# Revit family: Closet_Support_0250D_JRSmith
name_source: partatom
category: Plumbing Fixtures
revit_build: Autodesk Revit MEP 2012 (Build: 20110309_2315(x64)
units: mm (PartAtom-declared; Revit-internal decimal feet)

## types (5) — shared parameters
04 CSI = 22 05 29
95 CSI = 15050
Assembly Code = D2010120
Capacity = 300lb
Caulk Connection = Yes
Default Elevation = 0"
Description = Compact Fixture Supports with Vertical Offset Fittings for Siphon Jet Water Closets
E = 11 1/2"
Fixture Offset = 0"
LEED = Yes
Manufacturer = Jay R. Smith Mfg. Co.
Material = Cast Iron
Material Finish = Duco coated
No-Hub Connection = Yes
Offset From Base = 9"
OmniClass Code = 22-22 42 13
OmniClass Title = Commercial Water Closets, Urinals, and Bidets
Product URL = http://www.jrsmith.com
Radius = 3"
SMARTBIM Object Version = 3
SMARTBIM URL = www.smartbim.com
Stud Length = 9"
Technical and Installation = http://www.jrsmith.com
URL = http://www.jrsmith.com
Vent Connection = Yes
Vent Radius = 1 1/8"
Warranty = 1 year material and workmanship
zero-valued in all types: Max.Static Load Lbs

## per-type parameters (varying)
| type | Barrel Base | Inner Radius | Model | Nipple Length | Pipe Diameter | Pipe Diameter2 | Pipe Radius 1 | Pipe Radius 2 | Top Pipe Radius | Weight (lb) |
| 0250DY-5X5 | 4 1/2" | 2 1/4" | 0250Y-6X5 | 11 1/2" | 5" | 5" | 2 1/2" | 2 1/2" | 1 1/4" | 145.5 |
| 0250DY-6X4 | 4 1/2" | 2 3/4" | 0250Y-6X4 | 11 1/2" | 6" | 4" | 3" | 2" | 1 1/2" | 145.5 |
| 0250DY-4X4 | 4" | 1 3/4" | 0250Y-4X4 | 9" | 4" | 4" | 2" | 2" | 1" | 120.9 |
| 0250DY-6X5 | 4 1/2" | 2 3/4" | 0250Y-6X5 | 11 1/2" | 6" | 5" | 3" | 2 1/2" | 1 1/2" | 145.5 |
| 0250DY-5X4 | 4 1/2" | 2 1/4" | 0250Y-5X4 | 11 1/2" | 5" | 4" | 2 1/2" | 2" | 1 1/4" | 156.5 |

## geometry (parser evidence)
native form markers: Blend x14, Sweep x12
no freeform markers — native parametric forms only
